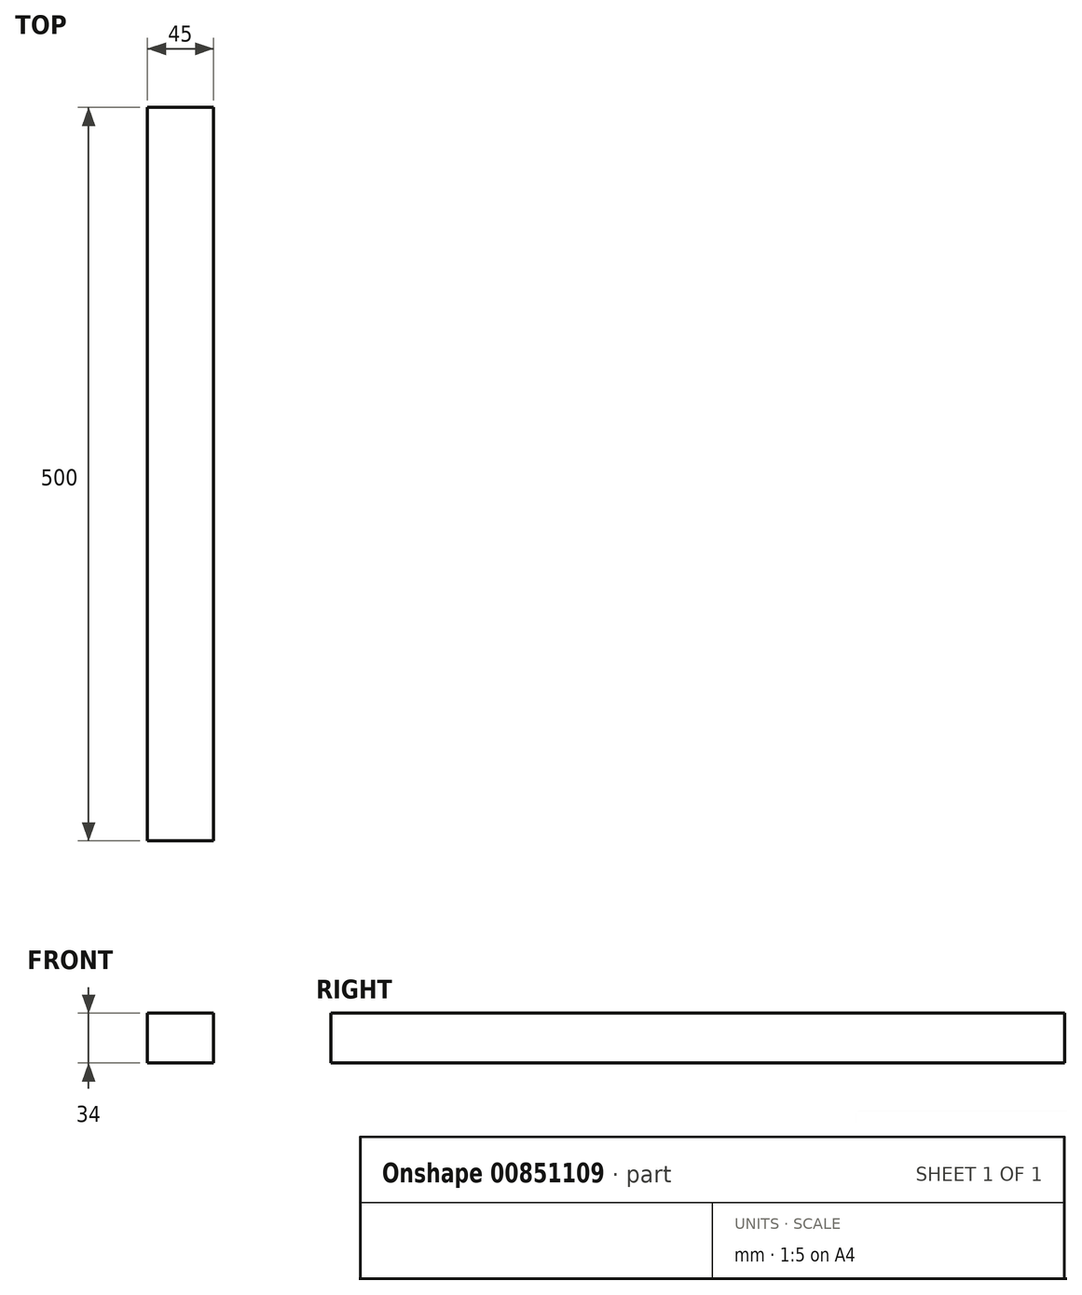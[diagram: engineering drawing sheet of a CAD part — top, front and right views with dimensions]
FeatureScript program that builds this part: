
annotation { "Feature Type Name" : "Feature", "Feature Type Description" : "" }
export const myFeature = defineFeature(function(context is Context, id is Id, definition is map)
    precondition{}
    {
        {
            var Q0;
            Q0=qCreatedBy(makeId("Front.planeOp"),FACE);
            var sketch = newSketch(context, id + "F0", { "sketchPlane" : qUnion([Q0])});
            skLineSegment(sketch, "E0.bottom", {"start": v(0, 0) * mm, "end": v(45, 0) * mm});
            skLineSegment(sketch, "E0.top", {"start": v(0, 34) * mm, "end": v(45, 34) * mm});
            skLineSegment(sketch, "E0.left", {"start": v(0, 0) * mm, "end": v(0, 34) * mm});
            skLineSegment(sketch, "E0.right", {"start": v(45, 0) * mm, "end": v(45, 34) * mm});
            skSolve(sketch);
        }
        {
            var Q0;
            Q0 = qSketchRegion(id + "F0", true);
            extrude(context, id + "F1", {"entities" : qUnion([Q0]), "depth" : 500 * mm, "offsetDistance" : 25.4 * mm});
        }
    });
